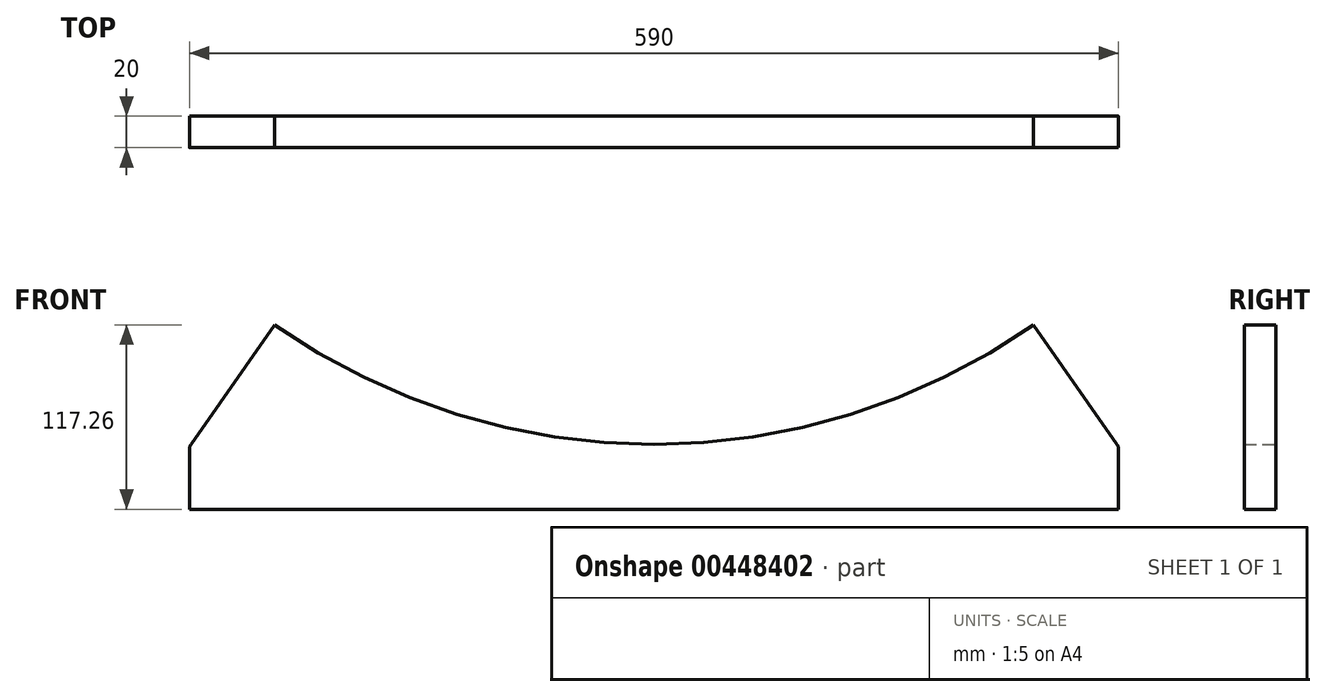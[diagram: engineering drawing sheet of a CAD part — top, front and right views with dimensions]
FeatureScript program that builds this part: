
annotation { "Feature Type Name" : "Feature", "Feature Type Description" : "" }
export const myFeature = defineFeature(function(context is Context, id is Id, definition is map)
    precondition{}
    {
        {
            var Q0;
            Q0=qCreatedBy(makeId("Front.planeOp"),FACE);
            var sketch = newSketch(context, id + "F0", { "sketchPlane" : qUnion([Q0])});
            skLineSegment(sketch, "E0", {"start": v(-295, 0) * mm, "end": v(295, 0) * mm});
            skLineSegment(sketch, "E1", {"start": v(-295, 0) * mm, "end": v(-295, 40) * mm});
            skLineSegment(sketch, "E2", {"start": v(0, 0) * mm, "end": v(0, 461.3) * mm, "construction": true});
            skLineSegment(sketch, "E3", {"start": v(-295, 40) * mm, "end": v(-240.9, 117.26) * mm});
            skLineSegment(sketch, "E4.MirrorCS", {"start": v(295, 40) * mm, "end": v(240.9, 117.26) * mm});
            skLineSegment(sketch, "E5.MirrorCS", {"start": v(295, 0) * mm, "end": v(295, 40) * mm});
            skLineSegment(sketch, "E6", {"start": v(0, 461.3) * mm, "end": v(-240.9, 117.26) * mm, "construction": true});
            skArc(sketch, "E7", {"start": v(-240.9, 117.26) * mm, "mid": v(0, 41.3) * mm, "end": v(240.9, 117.26) * mm});
            skSolve(sketch);
        }
        {
            var Q0;
            Q0=makeQuery(id+"F0.imprint","IMPRINT",FACE,{"disambiguationData":[TD([[makeQuery(id+"F0.imprint","IMPRINT",EDGE,{"derivedFrom":sQuery(id+"F0.wireOp",EDGE,"E0")}),1.0]])]});
            extrude(context, id + "F1", {"entities" : qUnion([Q0]), "depth" : 20 * mm});
        }
        {
            var Q0;
            Q0=makeQuery(id+"F1.opExtrude","SWEPT_EDGE",EDGE,{"disambiguationData":[OSD([sQuery(id+"F0.wireOp",EDGE,"E1"),sQuery(id+"F0.wireOp",EDGE,"E3")])]});
            var Q1;
            Q1=makeQuery(id+"F1.opExtrude","SWEPT_EDGE",EDGE,{"disambiguationData":[OSD([sQuery(id+"F0.wireOp",EDGE,"E4.MirrorCS"),sQuery(id+"F0.wireOp",EDGE,"E5.MirrorCS")])]});
            fillet(context, id + "F2", {"entities" : qUnion([Q0, Q1]), "radius" : 5 * mm, "tangentPropagation" : true, "allowEdgeOverflow" : false});
        }
    });
